# Revit family: Deca_Tábua para cozinha_Tábuas_AC.300.40
name_source: partatom
category: Plumbing Fixtures
units: mm (PartAtom-declared; Revit-internal decimal feet)

## family parameters
Cut with Voids When Loaded = No
Host = Face
Part Type = Normal
Room Calculation Point = No
Round Connector Dimension = Use Diameter
Shared = No

## types (1)
- AC.300.40.STEP_Preto
    Acompanha o Produto = -
    Aprovado por = quattroD
    Atendimento ao Cliente = 0800-0117073
    Categoria = ACESSORIOS COZINHA
    Composição Anel Vedação = -
    Composição Assento = -
    Composição Básica = Plástico de Engenharia
    Composição Componente = -
    Consumo = -
    Cor Interna = -
    Cor Principal = Preto
    Cor Secundária = -
    Cores Componente = -
    Criado por = quattroD
    Código Pai = AC.300.40
    Default Elevation = 0 mm  [stored 0 ft]
    Description = Tábua para cozinha
    Informações Complementares = -
    Itens de Instalação = -
    Linha = Acessórios de Inox
    Manufacturer = Deca
    Material = Deca_Preto
    Model = AC.300.40.STEP
    Norma = Não Possui
    Peso Líquido (Kg) = 0.42
    Pressão máx. funcionamento = -
    Pressão mín. Aquec. Acúmulo = -
    Pressão mín. Aquec. Passagem = -
    Pressão mín. funcionamento = -
    Saída de Esgoto = -
    Segmento = Banheiro Luxo
    Tipo de dispositivo economizador = -
    Tipo de mecanismo utilizado = -
    Tipo de rosca de entrada = -
    Tipo de rosca de saída = -
    URL = www.deca.com.br
    Vazão na Pressão máx. (L/min) = -
    Vazão na Pressão mín. (L/min) = -

note: [stored X ft] marks values corroborated as IEEE doubles in the binary element streams (Revit-internal decimal feet)

## geometry (parser evidence)
native form markers: Sweep x3
no freeform markers — native parametric forms only
